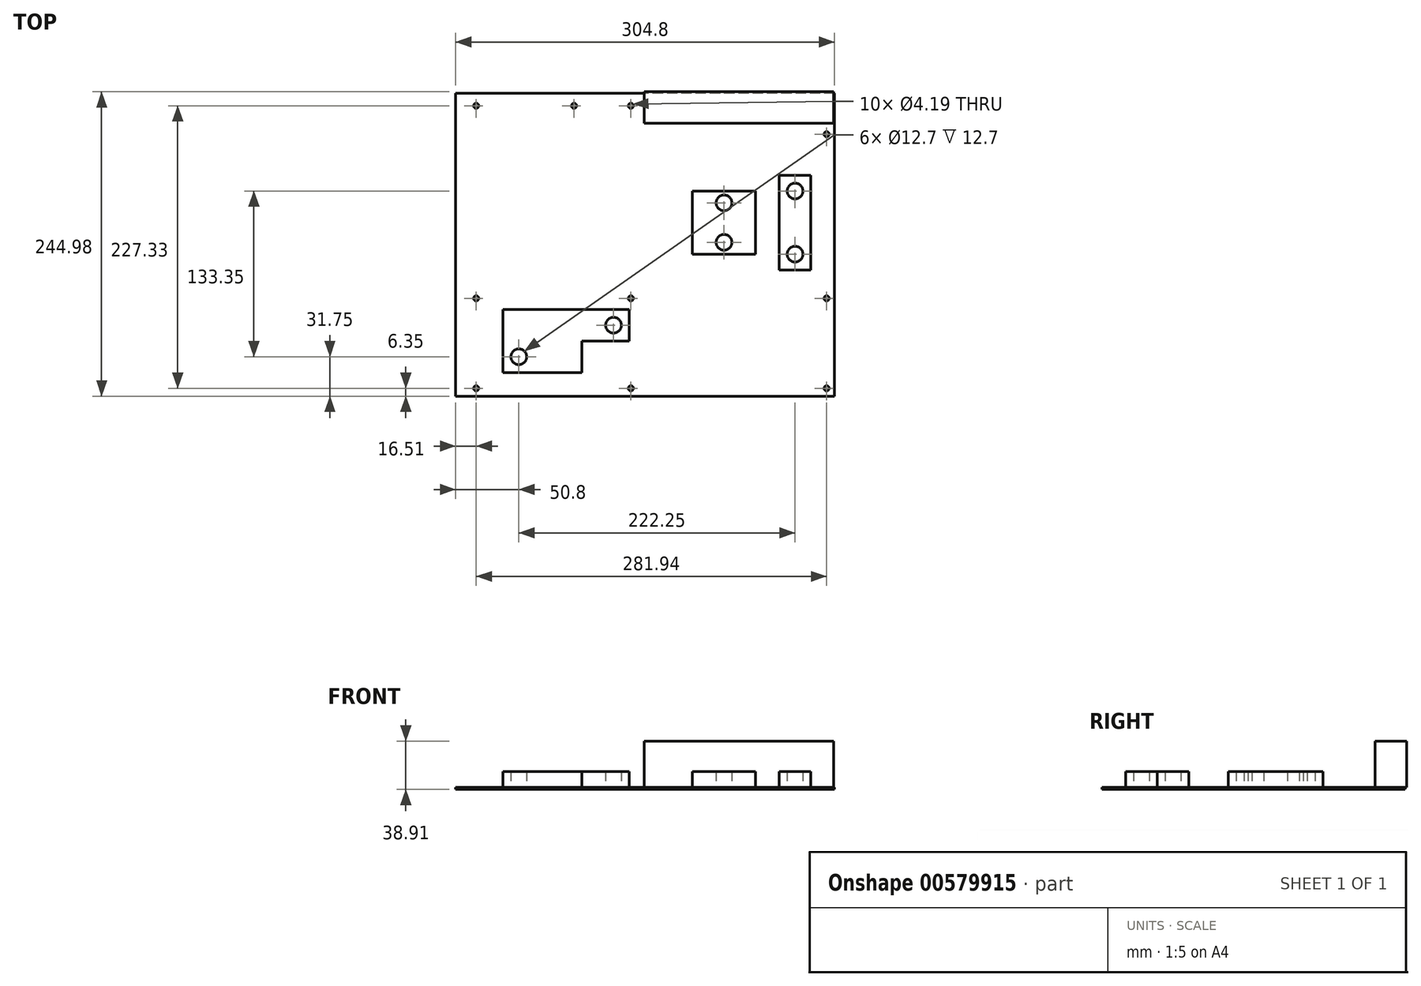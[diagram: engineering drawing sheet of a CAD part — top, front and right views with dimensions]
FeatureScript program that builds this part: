
annotation { "Feature Type Name" : "Feature", "Feature Type Description" : "" }
export const myFeature = defineFeature(function(context is Context, id is Id, definition is map)
    precondition{}
    {
        {
            var Q0;
            Q0=qCreatedBy(makeId("Top.planeOp"),FACE);
            var sketch = newSketch(context, id + "F0", { "sketchPlane" : qUnion([Q0])});
            skLineSegment(sketch, "E0.bottom", {"start": v(0, 0) * mm, "end": v(-304.8, 0) * mm});
            skLineSegment(sketch, "E0.top", {"start": v(0, 243.84) * mm, "end": v(-304.8, 243.84) * mm});
            skLineSegment(sketch, "E0.left", {"start": v(0, 0) * mm, "end": v(0, 243.84) * mm});
            skLineSegment(sketch, "E0.right", {"start": v(-304.8, 0) * mm, "end": v(-304.8, 243.84) * mm});
            skCircle(sketch, "E1", {"center": v(-288.29, 233.68) * mm, "radius": 2.1 * mm});
            skCircle(sketch, "E2", {"center": v(-288.29, 78.74) * mm, "radius": 2.1 * mm});
            skCircle(sketch, "E3", {"center": v(-288.29, 6.35) * mm, "radius": 2.1 * mm});
            skCircle(sketch, "E4", {"center": v(-209.55, 233.68) * mm, "radius": 2.1 * mm});
            skCircle(sketch, "E5", {"center": v(-163.83, 233.68) * mm, "radius": 2.1 * mm});
            skCircle(sketch, "E6", {"center": v(-163.83, 78.74) * mm, "radius": 2.1 * mm});
            skCircle(sketch, "E7", {"center": v(-163.83, 6.35) * mm, "radius": 2.1 * mm});
            skCircle(sketch, "E8", {"center": v(-6.35, 210.82) * mm, "radius": 2.1 * mm});
            skCircle(sketch, "E9", {"center": v(-6.35, 78.74) * mm, "radius": 2.1 * mm});
            skCircle(sketch, "E10", {"center": v(-6.35, 6.35) * mm, "radius": 2.1 * mm});
            skSolve(sketch);
        }
        {
            var Q0;
            Q0 = qSketchRegion(id + "F0", true);
            extrude(context, id + "F1", {"entities" : qUnion([Q0]), "depth" : 1.57 * mm, "offsetDistance" : 25.4 * mm});
        }
        {
            var Q0;
            Q0=makeQuery(id+"F1.opExtrude","CAP_FACE",FACE,{"disambiguationData":[OSD([sQuery(id+"F0.wireOp",EDGE,"E0.bottom"),sQuery(id+"F0.wireOp",EDGE,"E0.top"),sQuery(id+"F0.wireOp",EDGE,"E0.left"),sQuery(id+"F0.wireOp",EDGE,"E0.right"),sQuery(id+"F0.wireOp",EDGE,"E1"),sQuery(id+"F0.wireOp",EDGE,"E2"),sQuery(id+"F0.wireOp",EDGE,"E3"),sQuery(id+"F0.wireOp",EDGE,"E4"),sQuery(id+"F0.wireOp",EDGE,"E5"),sQuery(id+"F0.wireOp",EDGE,"E6"),sQuery(id+"F0.wireOp",EDGE,"E7"),sQuery(id+"F0.wireOp",EDGE,"E8"),sQuery(id+"F0.wireOp",EDGE,"E9"),sQuery(id+"F0.wireOp",EDGE,"E10")])],"isStart":false});
            var sketch = newSketch(context, id + "F2", { "sketchPlane" : qUnion([Q0])});
            skLineSegment(sketch, "E11.bottom", {"start": v(-0.86, 219.58) * mm, "end": v(-153, 219.58) * mm});
            skLineSegment(sketch, "E11.top", {"start": v(-0.86, 244.98) * mm, "end": v(-153, 244.98) * mm});
            skLineSegment(sketch, "E11.left", {"start": v(-0.86, 219.58) * mm, "end": v(-0.86, 244.98) * mm});
            skLineSegment(sketch, "E11.right", {"start": v(-153, 219.58) * mm, "end": v(-153, 244.98) * mm});
            skPoint(sketch, "E12", {"position": v(-288.29, 233.68) * mm});
            skSolve(sketch);
        }
        {
            var Q0;
            Q0 = qSketchRegion(id + "F2", true);
            extrude(context, id + "F3", {"entities" : qUnion([Q0]), "operationType" : NewBodyOperationType.ADD, "depth" : 37.34 * mm, "offsetDistance" : 25.4 * mm});
        }
        {
            var Q0;
            Q0=makeQuery(id+"F1.opExtrude","CAP_FACE",FACE,{"disambiguationData":[OSD([sQuery(id+"F0.wireOp",EDGE,"E0.bottom"),sQuery(id+"F0.wireOp",EDGE,"E0.top"),sQuery(id+"F0.wireOp",EDGE,"E0.left"),sQuery(id+"F0.wireOp",EDGE,"E0.right"),sQuery(id+"F0.wireOp",EDGE,"E1"),sQuery(id+"F0.wireOp",EDGE,"E2"),sQuery(id+"F0.wireOp",EDGE,"E3"),sQuery(id+"F0.wireOp",EDGE,"E4"),sQuery(id+"F0.wireOp",EDGE,"E5"),sQuery(id+"F0.wireOp",EDGE,"E6"),sQuery(id+"F0.wireOp",EDGE,"E7"),sQuery(id+"F0.wireOp",EDGE,"E8"),sQuery(id+"F0.wireOp",EDGE,"E9"),sQuery(id+"F0.wireOp",EDGE,"E10")])],"isStart":false});
            var sketch = newSketch(context, id + "F4", { "sketchPlane" : qUnion([Q0])});
            skLineSegment(sketch, "E13.bottom", {"start": v(-114.3, 165.1) * mm, "end": v(-63.5, 165.1) * mm});
            skLineSegment(sketch, "E13.top", {"start": v(-114.3, 114.3) * mm, "end": v(-63.5, 114.3) * mm});
            skLineSegment(sketch, "E13.left", {"start": v(-114.3, 165.1) * mm, "end": v(-114.3, 114.3) * mm});
            skLineSegment(sketch, "E13.right", {"start": v(-63.5, 165.1) * mm, "end": v(-63.5, 114.3) * mm});
            skCircle(sketch, "E14", {"center": v(-88.9, 155.57) * mm, "radius": 6.35 * mm});
            skCircle(sketch, "E15", {"center": v(-88.9, 123.82) * mm, "radius": 6.35 * mm});
            skSolve(sketch);
        }
        {
            var Q0;
            Q0 = qSketchRegion(id + "F4", true);
            extrude(context, id + "F5", {"entities" : qUnion([Q0]), "operationType" : NewBodyOperationType.ADD, "depth" : 12.7 * mm, "offsetDistance" : 25.4 * mm});
        }
        {
            var Q0;
            {var subQ0=sQuery(id+"F0.wireOp",EDGE,"E5");var subQ1=sQuery(id+"F0.wireOp",EDGE,"E4");var subQ3=sQuery(id+"F0.wireOp",EDGE,"E3");var subQ5=sQuery(id+"F0.wireOp",EDGE,"E2");var subQ6=sQuery(id+"F0.wireOp",EDGE,"E1");var subQ7=sQuery(id+"F0.wireOp",EDGE,"E6");var subQ8=sQuery(id+"F0.wireOp",EDGE,"E0.bottom");var subQ9=sQuery(id+"F0.wireOp",EDGE,"E0.right");var subQ11=sQuery(id+"F0.wireOp",EDGE,"E0.top");var subQ12=sQuery(id+"F0.wireOp",EDGE,"E0.left");var subQ13=sQuery(id+"F0.wireOp",EDGE,"E7");var subQ14=sQuery(id+"F0.wireOp",EDGE,"E8");var subQ15=sQuery(id+"F0.wireOp",EDGE,"E9");var subQ16=sQuery(id+"F0.wireOp",EDGE,"E10");Q0=makeQuery(id+"F5.boolean.opBoolean","SPLIT",FACE,{"disambiguationData":[TD([makeQuery(id+"F1.opExtrude","SWEPT_FACE",FACE,{"disambiguationData":[OSD([subQ8])]})])],"derivedFrom":makeQuery(id+"F1.opExtrude","CAP_FACE",FACE,{"disambiguationData":[OSD([subQ8,subQ11,subQ12,subQ9,subQ6,subQ5,subQ3,subQ1,subQ0,subQ7,subQ13,subQ14,subQ15,subQ16])],"isStart":false})});}
            var sketch = newSketch(context, id + "F6", { "sketchPlane" : qUnion([Q0])});
            skLineSegment(sketch, "E16.bottom", {"start": v(-44.45, 177.8) * mm, "end": v(-19.05, 177.8) * mm});
            skLineSegment(sketch, "E16.top", {"start": v(-44.45, 101.6) * mm, "end": v(-19.05, 101.6) * mm});
            skLineSegment(sketch, "E16.left", {"start": v(-44.45, 177.8) * mm, "end": v(-44.45, 101.6) * mm});
            skLineSegment(sketch, "E16.right", {"start": v(-19.05, 177.8) * mm, "end": v(-19.05, 101.6) * mm});
            skCircle(sketch, "E17", {"center": v(-31.75, 165.1) * mm, "radius": 6.35 * mm});
            skCircle(sketch, "E18", {"center": v(-31.75, 114.3) * mm, "radius": 6.35 * mm});
            skSolve(sketch);
        }
        {
            var Q0;
            Q0 = qSketchRegion(id + "F6", true);
            extrude(context, id + "F7", {"entities" : qUnion([Q0]), "operationType" : NewBodyOperationType.ADD, "depth" : 12.7 * mm, "offsetDistance" : 25.4 * mm});
        }
        {
            var Q0;
            {var subQ4=sQuery(id+"F0.wireOp",EDGE,"E10");var subQ6=sQuery(id+"F0.wireOp",EDGE,"E9");var subQ8=sQuery(id+"F0.wireOp",EDGE,"E8");var subQ10=sQuery(id+"F0.wireOp",EDGE,"E7");var subQ14=sQuery(id+"F0.wireOp",EDGE,"E0.left");var subQ16=sQuery(id+"F0.wireOp",EDGE,"E0.top");var subQ21=sQuery(id+"F0.wireOp",EDGE,"E0.right");var subQ23=sQuery(id+"F0.wireOp",EDGE,"E0.bottom");var subQ24=makeQuery(id+"F1.opExtrude","SWEPT_FACE",FACE,{"disambiguationData":[OSD([subQ23])]});var subQ25=sQuery(id+"F0.wireOp",EDGE,"E6");var subQ27=sQuery(id+"F0.wireOp",EDGE,"E1");var subQ29=sQuery(id+"F0.wireOp",EDGE,"E2");var subQ32=sQuery(id+"F0.wireOp",EDGE,"E3");var subQ35=sQuery(id+"F0.wireOp",EDGE,"E4");var subQ37=sQuery(id+"F0.wireOp",EDGE,"E5");Q0=makeQuery(id+"F7.boolean.opBoolean","SPLIT",FACE,{"disambiguationData":[TD([subQ24])],"derivedFrom":makeQuery(id+"F5.boolean.opBoolean","SPLIT",FACE,{"disambiguationData":[TD([subQ24])],"derivedFrom":makeQuery(id+"F1.opExtrude","CAP_FACE",FACE,{"disambiguationData":[OSD([subQ23,subQ16,subQ14,subQ21,subQ27,subQ29,subQ32,subQ35,subQ37,subQ25,subQ10,subQ8,subQ6,subQ4])],"isStart":false})})});}
            var sketch = newSketch(context, id + "F8", { "sketchPlane" : qUnion([Q0])});
            skLineSegment(sketch, "E19", {"start": v(-266.7, 69.85) * mm, "end": v(-266.7, 19.05) * mm});
            skLineSegment(sketch, "E20", {"start": v(-266.7, 19.05) * mm, "end": v(-203.2, 19.05) * mm});
            skLineSegment(sketch, "E21", {"start": v(-203.2, 19.05) * mm, "end": v(-203.2, 44.45) * mm});
            skLineSegment(sketch, "E22", {"start": v(-203.2, 44.45) * mm, "end": v(-165.1, 44.45) * mm});
            skLineSegment(sketch, "E23", {"start": v(-165.1, 44.45) * mm, "end": v(-165.1, 69.85) * mm});
            skLineSegment(sketch, "E24", {"start": v(-165.1, 69.85) * mm, "end": v(-266.7, 69.85) * mm});
            skCircle(sketch, "E25", {"center": v(-177.8, 57.15) * mm, "radius": 6.35 * mm});
            skCircle(sketch, "E26", {"center": v(-254, 31.75) * mm, "radius": 6.35 * mm});
            skSolve(sketch);
        }
        {
            var Q0;
            Q0 = qSketchRegion(id + "F8", true);
            extrude(context, id + "F9", {"entities" : qUnion([Q0]), "operationType" : NewBodyOperationType.ADD, "depth" : 12.7 * mm, "offsetDistance" : 25.4 * mm});
        }
    });
